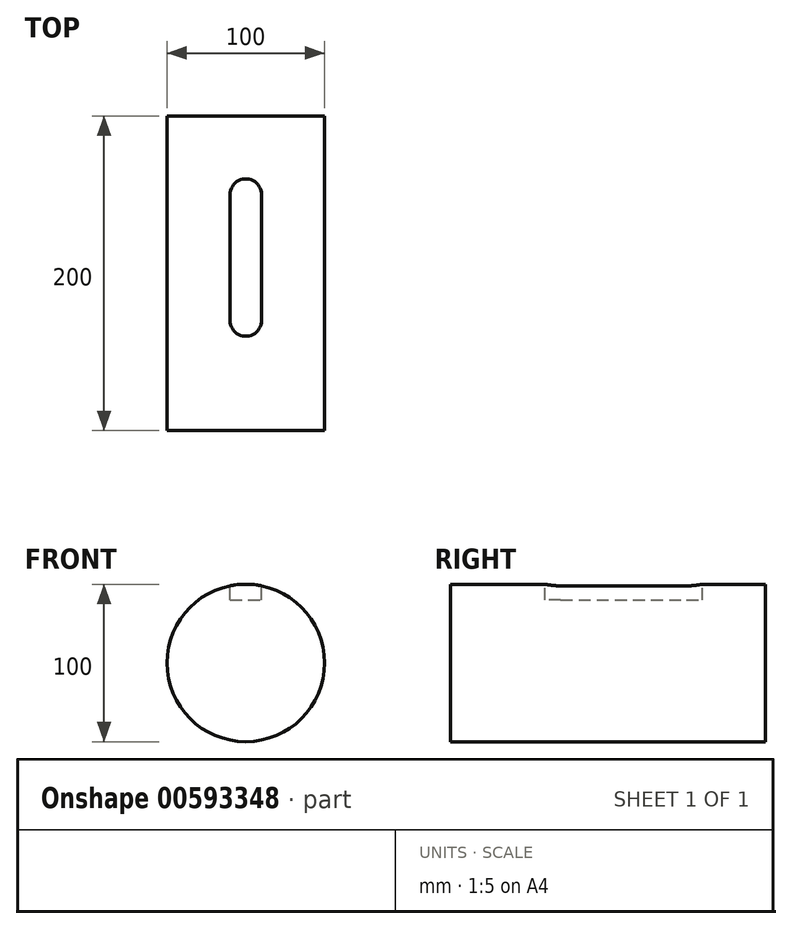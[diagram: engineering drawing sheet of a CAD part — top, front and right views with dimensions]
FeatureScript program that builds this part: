
annotation { "Feature Type Name" : "Feature", "Feature Type Description" : "" }
export const myFeature = defineFeature(function(context is Context, id is Id, definition is map)
    precondition{}
    {
        {
            var Q0;
            Q0=qCreatedBy(makeId("Front.planeOp"),FACE);
            var sketch = newSketch(context, id + "F0", { "sketchPlane" : qUnion([Q0])});
            skCircle(sketch, "E0", {"center": v(0, 0) * mm, "radius": 50 * mm});
            skSolve(sketch);
        }
        {
            var Q0;
            Q0 = qSketchRegion(id + "F0", true);
            extrude(context, id + "F1", {"entities" : qUnion([Q0]), "depth" : 200 * mm, "offsetDistance" : 25 * mm});
        }
        {
            var Q0;
            Q0=qCreatedBy(makeId("Top.planeOp"),FACE);
            cPlane(context, id + "F2", {"entities" : qUnion([Q0]), "cplaneType" : CPlaneType.OFFSET, "offset" : 50 * mm, "width" : 150 * mm, "height" : 150 * mm});
        }
        {
            var Q0;
            Q0=qCreatedBy(id+"F2.planeOp",FACE);
            var sketch = newSketch(context, id + "F3", { "sketchPlane" : qUnion([Q0])});
            skLineSegment(sketch, "E1", {"start": v(-10, -130) * mm, "end": v(-10, -50) * mm});
            skArc(sketch, "E2", {"start": v(10, -50) * mm, "mid": v(0, -40) * mm, "end": v(-10, -50) * mm});
            skLineSegment(sketch, "E3", {"start": v(10, -50) * mm, "end": v(10, -130) * mm});
            skArc(sketch, "E4", {"start": v(-10, -130) * mm, "mid": v(0, -140) * mm, "end": v(10, -130) * mm});
            skSolve(sketch);
        }
        {
            var Q0;
            Q0 = qSketchRegion(id + "F3", true);
            extrude(context, id + "F4", {"entities" : qUnion([Q0]), "operationType" : NewBodyOperationType.REMOVE, "oppositeDirection" : true, "depth" : 10 * mm, "offsetDistance" : 25 * mm});
        }
    });
